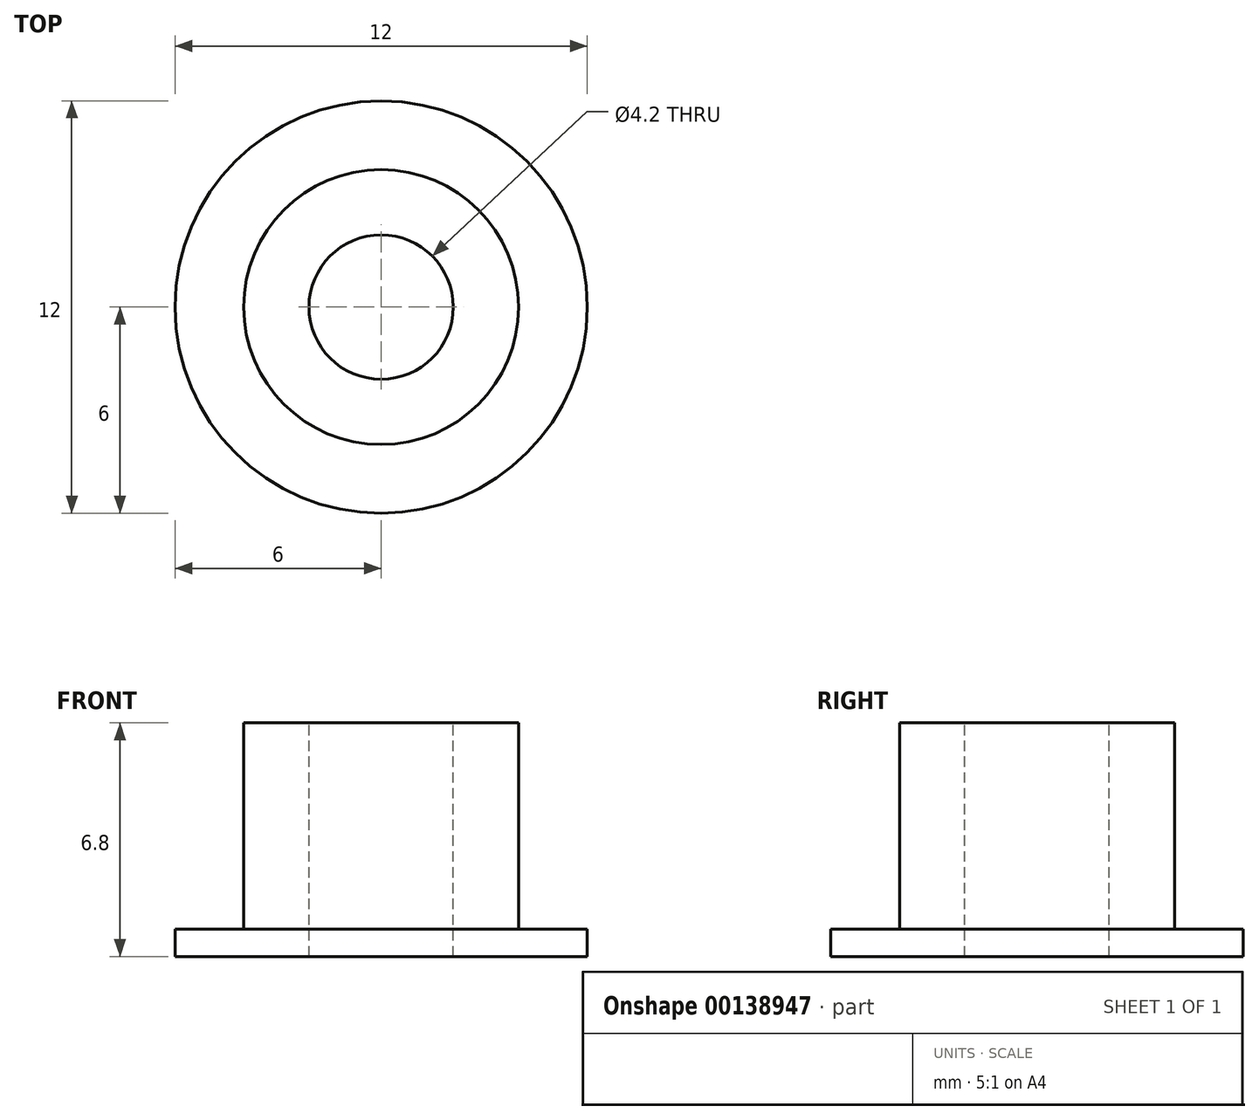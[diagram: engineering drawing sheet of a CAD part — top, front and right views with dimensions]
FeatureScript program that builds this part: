
annotation { "Feature Type Name" : "Feature", "Feature Type Description" : "" }
export const myFeature = defineFeature(function(context is Context, id is Id, definition is map)
    precondition{}
    {
        {
            var Q0;
            Q0=qCreatedBy(makeId("Right.planeOp"),FACE);
            var sketch = newSketch(context, id + "F0", { "sketchPlane" : qUnion([Q0])});
            skLineSegment(sketch, "E0", {"start": v(2.1, 0) * mm, "end": v(6, 0) * mm});
            skLineSegment(sketch, "E1", {"start": v(6, 0) * mm, "end": v(6, 0.8) * mm});
            skLineSegment(sketch, "E2", {"start": v(6, 0.8) * mm, "end": v(4, 0.8) * mm});
            skLineSegment(sketch, "E3", {"start": v(4, 0.8) * mm, "end": v(4, 6.8) * mm});
            skLineSegment(sketch, "E4", {"start": v(2.1, 6.8) * mm, "end": v(2.1, 0) * mm});
            skLineSegment(sketch, "E5", {"start": v(4, 6.8) * mm, "end": v(2.1, 6.8) * mm});
            skLineSegment(sketch, "E6", {"start": v(0, 12.27) * mm, "end": v(0, -5.12) * mm, "construction": true});
            skSolve(sketch);
        }
        {
            var Q0;
            Q0=makeQuery(id+"F0.imprint","IMPRINT",FACE,{"disambiguationData":[TD([[makeQuery(id+"F0.imprint","IMPRINT",EDGE,{"derivedFrom":sQuery(id+"F0.wireOp",EDGE,"E0")}),1.0]])]});
            var Q1;
            Q1=sQuery(id+"F0.wireOp",EDGE,"E6");
            revolve(context, id + "F1", {"entities" : qUnion([Q0]), "axis" : qUnion([Q1]), "revolveType" : RevolveType.FULL});
        }
    });
